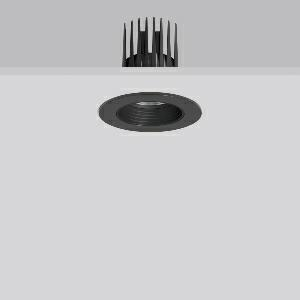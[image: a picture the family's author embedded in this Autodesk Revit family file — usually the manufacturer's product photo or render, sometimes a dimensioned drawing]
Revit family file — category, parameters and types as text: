
# Revit family: heledon_mini_e_901753_003_1_362d
name_source: partatom
category: Lighting Fixtures
units: mm (PartAtom-declared; Revit-internal decimal feet)

## family parameters
Cut with Voids When Loaded = No
Host = Face
Light Source = No
Part Type = Normal
Room Calculation Point = No
Round Connector Dimension = Use Diameter
Shared = No

## types (1)
- HELEDON mini E (1 x LED Modul 940, 3000 lm, 4000)
    Apparent Load = 29 VA
    Approval mark = CE
    CIE Flux Codes = 98 100 100 100 100
    Color Rendering = 92
    Color Temperature = 4000
    Default Elevation = 1800 mm
    Description = Series: HELEDON mini
Round recessed downlight. Housing: die-cast aluminium, powder-coated. Black plastic ring and recessed LED to prevent glare from the side. Optical assembly with lens made of plastic (polycarbonate) for the best homogeneous light distribution - can be changed without tools. Best colour rendering index Ra>90. Suitable for Recessed ceiling mounting. Installation without tools thanks to spring fastening system. Including separate LED converter with connecting cable 600 mm.High quality converter without flickering and stroboscopic effect. Through-wiring box (5 pole) available as accessory. The following accessories can be mounted without use of tools: interchangeable lenses, decorative glasses, honeycomb louvre, clear and frosted diffusers, white interchangeable plastic ring. 
Colour: deep black, matt (RAL 9005)
Diameter: 124 mm
Height: 3 mm
Cut-out diameter: 114 mm
Recess height: 170 mm
Luminaire: recess height: 120 mm
Lamp: LED
Socket: without socket
Colour temperature: 4000K
Colour rendering index (CRI): 92
System power: 29 W
Rated luminous flux: 3000 lm
Luminous efficiency: 103 lm/W
Control gear: Regulated power supply
Protection class: II
Type of protection: IP 20
    Height = 0 mm  [stored 0 ft]
    Lamp = 1 x LED Modul 940
    Lamp Light Flux = 3000 lm
    Lamp count = 1
    Length = 124 mm  [stored 0.406824 ft]
    Lifetime = 50000 h
    Luminous efficacy = 103 lm/W
    Manufacturer = RZB
    ModVariant = No
    Model = 901753.003.1
    Mounting Place = Ceiling
    Mounting Type = Recessed
    Number of Poles = 1
    OnlyDefault = Yes
    Power Factor = 1
    Product Name = HELEDON mini E
    Product group = Recessed downlights
    ProductGroupID = 402
    Protection Class = Protection class II
    Protection Degree = IP 20
    RLX_Detail_Level = 1
    RLX_Emergency_Light_Flux = 0 lm
    RLX_Emergency_Type = 0
    RLX_Emergency_Type_DB = No
    RlxData = <blob elided: 127649 chars, md5=147a66e4>
    Socket = socket
    Standby Power = 0 W
    System Light Flux = 3000 lm
    System Power = 29 W
    Type Comments = Product without accessories
    Type Image = 901656.003.jpg
    URL = http://relux.com
    VarID = ---
    Voltage = 230 V
    Voltage Range = 220-240 V
    Weight = 0.00 kg
    Width = 0 mm  [stored 0 ft]

note: [stored X ft] marks values corroborated as IEEE doubles in the binary element streams (Revit-internal decimal feet)

## geometry (parser evidence)
native form markers: Blend x4, Sweep x11
no freeform markers — native parametric forms only
